# Revit family: 2019_ES_Ventana_Qsystems_Q120_2-Hojas-Corredera
name_source: partatom
category: Windows
units: mm (PartAtom-declared; Revit-internal decimal feet)

## family parameters
Always vertical = Yes
Cut with Voids When Loaded = No
Host = Wall
OmniClass Number = 23.30.20.14.11
OmniClass Title = Metal Windows
Room Calculation Point = No
Shared = No

## types (2) — shared parameters
Acabado = Lacado, anodizado, madera
Acristalamiento = Cristal - Vidrio claro templado 6/18/6
Altura Real = 2.800 m
Altura de antepecho por defecto = 0.000 m
Altura maxima = 3.750 m
Altura minima = 0.600 m
Analytic Construction = <None>
Ancho Marco Central = 0.103 m
Ancho Marco Lateral = 0.140 m
Ancho Marco Superior Inferior = 0.140 m
Ancho Vidrio = 1.309 m
AnchoPoliamidaHoja = 0.016 m
AnchoPoliamidaMarco = 0.034 m
Anchura Maxima = 3.350 m
Anchura Minima = 0.600 m
Anchura Real = 3.000 m
Area = 8.40 m²
Autor = Bimetica Parametric Design Services S.L.
BIMsupport = https://bimsupport.info
COBieCategoria = IfcWindow
Catálogo (URL) = https://qsystemsaluminio.com
CerramientoExterior = Yes
Clasificacion acustica = 29 (-1;-2) dB
ConfiguracionPoliamidas = 964000 - 268400
ControlHumos = No
Description = Ventana corredera de 3 hojas, dos railes
Desfase Exterior = 0.000 m
Desfase Interior = 0.000 m
EstanqueidadAgua = 7A
FechaEmisionElementoBIM = 01/12/2021
FechaVencimientoElementoBIM = 01/12/2022
Fraccion de area de acristalamiento = 0.7851
GrosorMarco = 0.122 m
GrosorMaximoAcristalamiento = 0.040 m
GrosorMinimoAcristalamiento = 0.000 m
Gubimclass Codigo = 30.10.20.10
Gubimclass Titulo = Ventanas de fachadas
Height = 2.800 m
Historial = (RVT2019) Creación del Elemento.
IfcExportAs = IfcWindow
IfcExportType = Ventana Corredera
InformacionTecnica = https://qsystemsaluminio.com
Intercalario = Technoform Warm Edge
Manilla = Plástico, negro opaco
Manufacturer = QSystems
Marcado CE = No
Marco = Aluminio Anodizado, lacado
MasterformatCodigo = 08 51 13
MasterformatTitulo = Aluminum Windows
Model = Corredera Q120 Inglete 2 hojas correderas
Motorizada = No
Numero de Licencia = XXX-XXXX9536
OmniclassCodigo = 23-17 13 13 13
OmniclassTitulo = Metal Horizontal Sliding Windows
Operation = Corredera
Perimetro = 8.602 m
PermeabilidadAlAire = Clase 4
Peso = 0.00 kg
Plataforma descaga contenido BIM = www.bimetica.com
Poliamida = Technoform polyamide
Profundidad = 0.122 m
PuntoDeContacto = QSystems
Referencia = Q120
ReferenciaContacto = QSystems
RepisaExterior = Yes
RepisaInterior = Yes
ResistenciaAlViento = C5
Rough Height = 2.810 m
Rough Width = 3.010 m
SalidaEmergencia = Yes
Serie = Q120
TelefonoContacto = +34 91 895 58 00
Titular = Alueuropa S.A.
Total Y𝑔 = 0.049
Total 𝐴𝑓 = 1.808765
Total 𝐴𝑔 = 6.59484
Total 𝑈𝑔 = 1.8
Total 𝑙𝑔 = 15.314
UNSPSCCodigo = 30171607
UNSPSCTitulo = Horizontal slider windows
URL = https://qsystemsaluminio.com
URL Perfil BIM = https://bimetica.com
URL Poliamida - Catálogo = http://www.technoform.com
URLProducto = https://qsystemsaluminio.com
Uniclass2.0Codigo = 25-30-95-78
Uniclass2.0Titulo = Sliding window systems
Version = RVT2019
Version Estandar GDO-BIM = GDO-BIM V02
Wall Closure = Both
Width = 3.000 m
Y𝑔 = 0.750386
Y𝑔 P1e = 0.049
Y𝑔 P1i = 0.049
Y𝑔 P2e = 0.049
Y𝑔 P2i = 0.049
Y𝑔 P3e = 0.049
Y𝑔 P3i = 0.049
Y𝑔 P4 = 0.049
𝐴𝑓 P1e = 0.20 m²
𝐴𝑓 P1i = 0.20 m²
𝐴𝑓 P2e = 0.20 m²
𝐴𝑓 P2i = 0.20 m²
𝐴𝑓 P3e = 0.37 m²
𝐴𝑓 P3i = 0.37 m²
𝐴𝑓 P4 = 0.28 m²
𝐴𝑔 e = 3.30 m²
𝐴𝑔 i = 3.30 m²
𝑈𝑓 P4 = 5.1
𝑈𝑔 e = 1.8
𝑈𝑔 i = 1.8
𝑙𝑔 P1e = 1.3085
𝑙𝑔 P1i = 1.3085
𝑙𝑔 P2e = 1.3085
𝑙𝑔 P2i = 1.3085
𝑙𝑔 P3e = 2.52
𝑙𝑔 P3i = 2.52
𝑙𝑔 P4 = 5.04
zero-valued in all types: AcidificacionAtmosfericaPorUnidad, AguaConsumidaPorUnidad, CambioClimaticoPorUnidad, CosteMantenimiento, DestruccionCapaOzonoEstratosfericaPorUnidad, Energia consumida, EnergiaNoRenovableConsumidaPorUnidad, EnergiaPrimariaTotalConsumidaPorUnidad, EnergiaRenovableConsumidaPorUnidad, EutrofizacionPorUnidad, FaltaDeRecursosPorUnidad, FormacionFotoquimicaOzonoPorUnidad, Infiltracion, ResiduoInertePorUnidad, ResiduoRadioactivoPorUnidad, ResiduosNoPeligrososPorUnidad, ResiduosPeligrososPorUnidad

## per-type parameters (varying)
| type | Espuma | Heat Transfer Coefficient (U) | Total 𝑈𝑓 | Transmitancia termica | URL Poliamida | 𝑈𝑓 P1e | 𝑈𝑓 P1i | 𝑈𝑓 P2e | 𝑈𝑓 P2i | 𝑈𝑓 P3e | 𝑈𝑓 P3i | 𝑈𝑤 |
| 3000 x 2800 mm |  | 2.2898 W/(m²·K) | 3.660893 | 2.2898 W/(m²·K) | http://www.technoform.es
http://www.technoform.es | 3.4 | 3.4 | 3.4 | 3.4 | 3.4 | 3.4 | 2.289826 |
| 3000 x 2800 mm, con Espuma | Espuma de conductividad 0.021W/mK entre varillas.
Espuma de conductividad 0.036W/mK en el galce del vidrio. | 2.2352 W/(m²·K) | 3.406933 | 2.2352 W/(m²·K) |  | 3.1 | 3.1 | 3.1 | 3.1 | 3.1 | 3.1 | 2.235164 |

## geometry (parser evidence)
native form markers: Blend x2
no freeform markers — native parametric forms only
